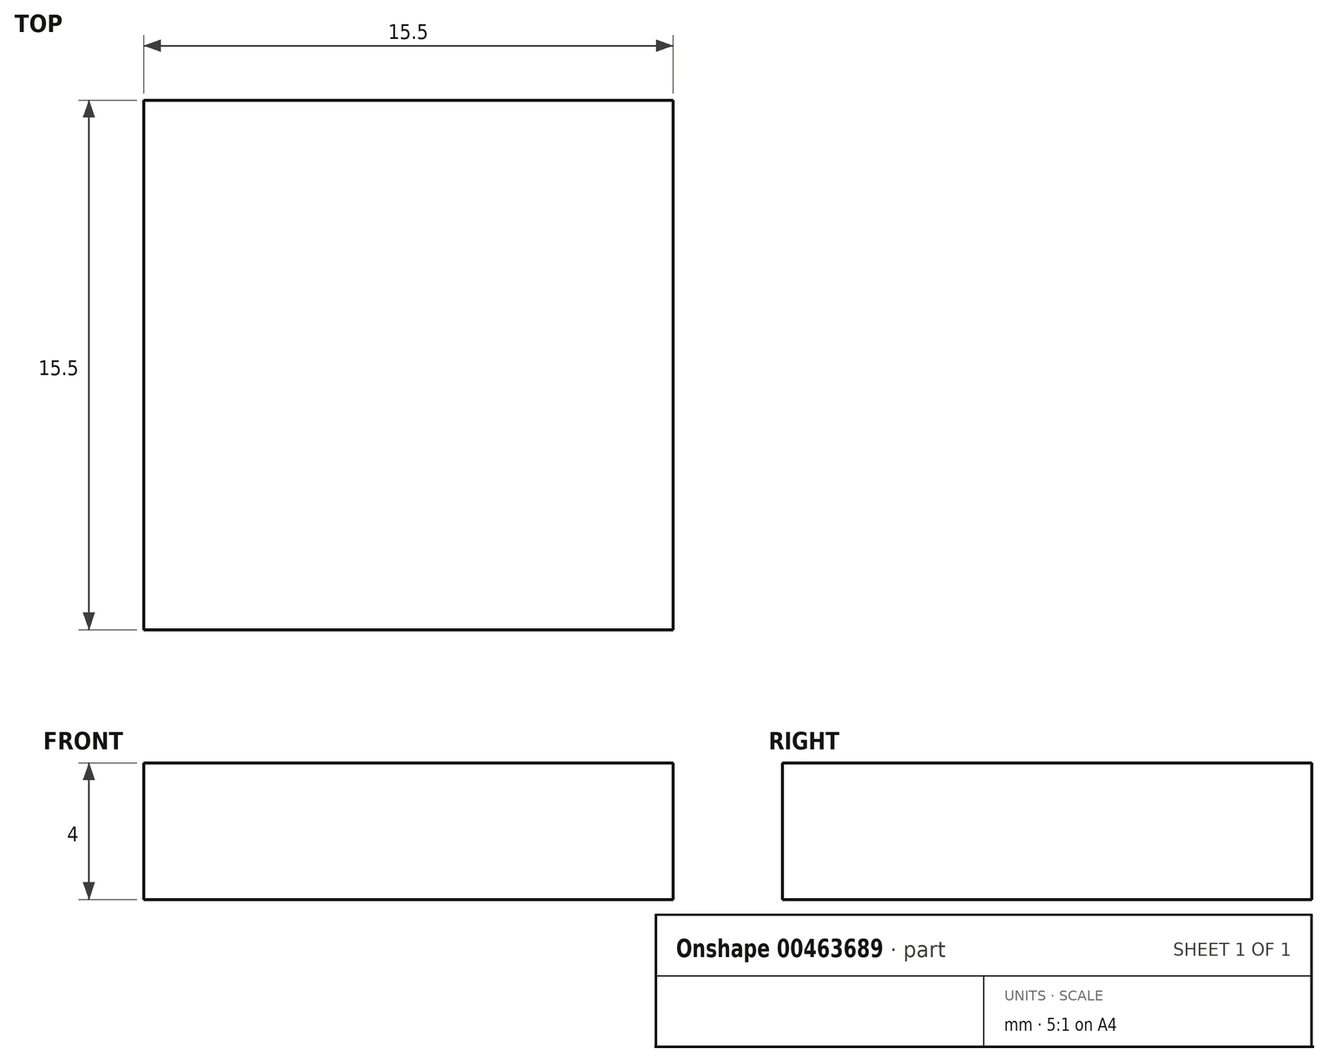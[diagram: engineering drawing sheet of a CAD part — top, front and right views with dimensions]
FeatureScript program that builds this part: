
annotation { "Feature Type Name" : "Feature", "Feature Type Description" : "" }
export const myFeature = defineFeature(function(context is Context, id is Id, definition is map)
    precondition{}
    {
        {
            var Q0;
            Q0=qCreatedBy(makeId("Top.planeOp"),FACE);
            var sketch = newSketch(context, id + "F0", { "sketchPlane" : qUnion([Q0])});
            skLineSegment(sketch, "E0.bottom", {"start": v(-7.75, 7.75) * mm, "end": v(7.75, 7.75) * mm});
            skLineSegment(sketch, "E0.top", {"start": v(-7.75, -7.75) * mm, "end": v(7.75, -7.75) * mm});
            skLineSegment(sketch, "E0.left", {"start": v(-7.75, 7.75) * mm, "end": v(-7.75, -7.75) * mm});
            skLineSegment(sketch, "E0.right", {"start": v(7.75, 7.75) * mm, "end": v(7.75, -7.75) * mm});
            skPoint(sketch, "E0.middle", {"position": v(0, 0) * mm});
            skSolve(sketch);
        }
        {
            var Q0;
            Q0 = qSketchRegion(id + "F0", true);
            extrude(context, id + "F1", {"entities" : qUnion([Q0]), "depth" : 4 * mm});
        }
    });
